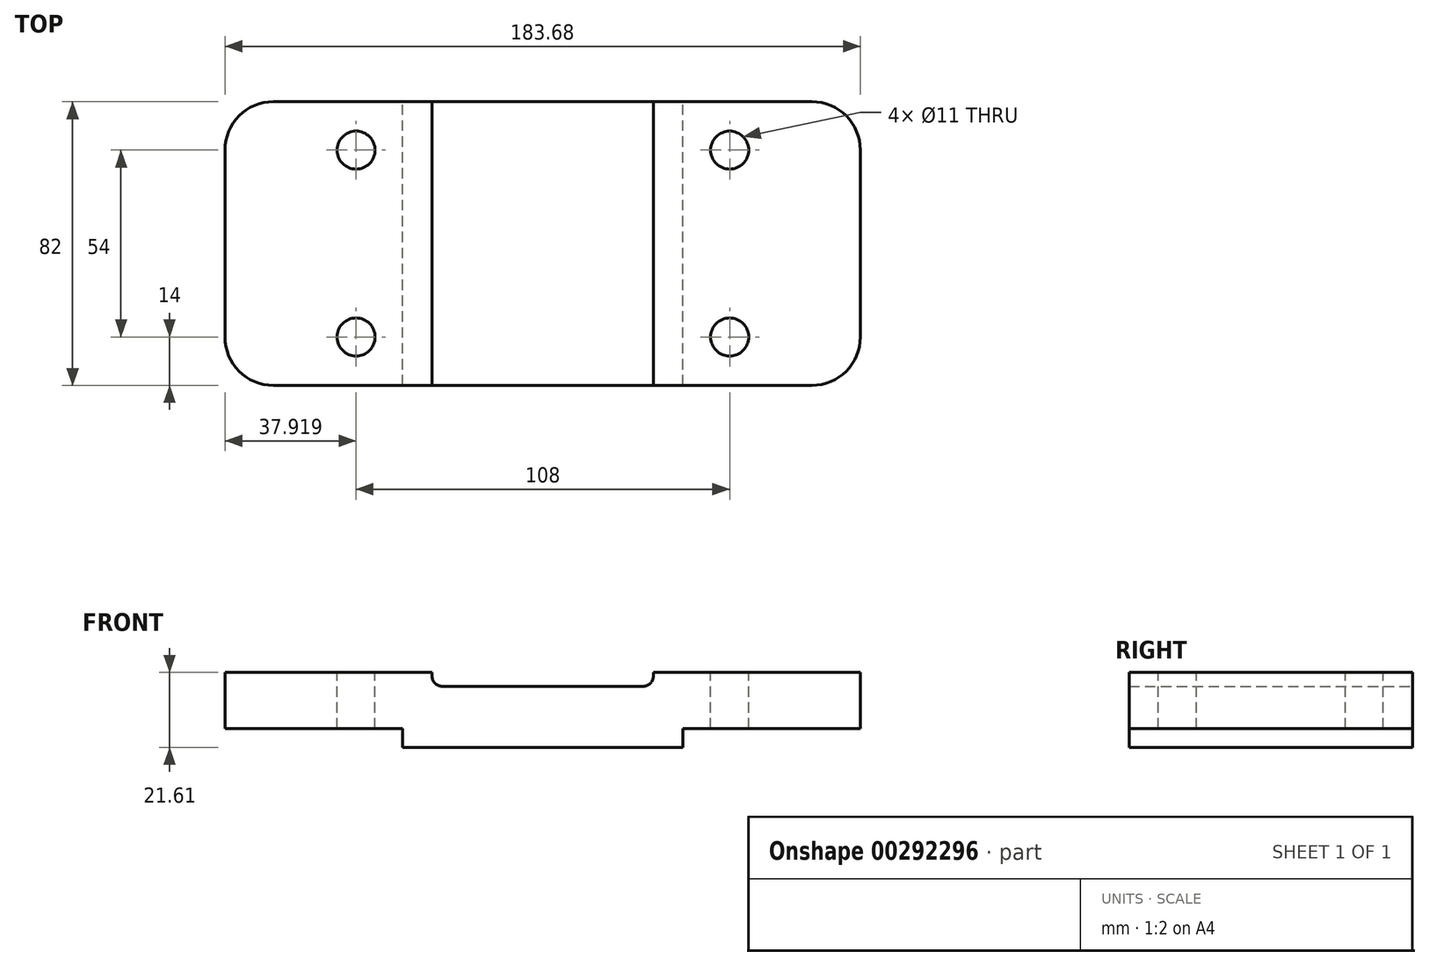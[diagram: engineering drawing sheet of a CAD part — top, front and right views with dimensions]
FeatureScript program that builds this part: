
annotation { "Feature Type Name" : "Feature", "Feature Type Description" : "" }
export const myFeature = defineFeature(function(context is Context, id is Id, definition is map)
    precondition{}
    {
        {
            var Q0;
            Q0=qCreatedBy(makeId("Front.planeOp"),FACE);
            var sketch = newSketch(context, id + "F0", { "sketchPlane" : qUnion([Q0])});
            skLineSegment(sketch, "E0.bottom", {"start": v(0, 0) * mm, "end": v(0, 0) * mm});
            skLineSegment(sketch, "E1", {"start": v(0, 0) * mm, "end": v(0, 21.6) * mm});
            skLineSegment(sketch, "E2", {"start": v(0, 21.6) * mm, "end": v(59.84, 21.6) * mm});
            skLineSegment(sketch, "E3", {"start": v(183.68, 21.6) * mm, "end": v(183.68, 5.4) * mm});
            skLineSegment(sketch, "E4", {"start": v(132.36, 0) * mm, "end": v(51.32, 0) * mm});
            skLineSegment(sketch, "E5", {"start": v(91.84, 21.6) * mm, "end": v(91.84, 0) * mm, "construction": true});
            skLineSegment(sketch, "E6.top", {"start": v(0, 5.4) * mm, "end": v(51.32, 5.4) * mm});
            skLineSegment(sketch, "E6.right", {"start": v(51.32, 0) * mm, "end": v(51.32, 5.4) * mm});
            skLineSegment(sketch, "E7.top", {"start": v(183.68, 5.4) * mm, "end": v(132.36, 5.4) * mm});
            skLineSegment(sketch, "E7.right", {"start": v(132.36, 0) * mm, "end": v(132.36, 5.4) * mm});
            skPoint(sketch, "E8.orphan", {"position": v(183.68, 0) * mm});
            skLineSegment(sketch, "E9", {"start": v(123.84, 21.6) * mm, "end": v(123.84, 20.6) * mm});
            skLineSegment(sketch, "E10", {"start": v(120.84, 17.6) * mm, "end": v(62.88, 17.6) * mm});
            skLineSegment(sketch, "E11", {"start": v(59.88, 20.51) * mm, "end": v(59.84, 21.6) * mm});
            skPoint(sketch, "E12.MirrorCS.end.orphan", {"position": v(91.84, 21.6) * mm});
            skPoint(sketch, "E12.MirrorCS.start.orphan", {"position": v(123.84, 21.6) * mm});
            skPoint(sketch, "E13.MirrorCS.start.orphan", {"position": v(59.84, 21.6) * mm});
            skLineSegment(sketch, "E14.trimOffspring", {"start": v(123.84, 21.6) * mm, "end": v(183.68, 21.6) * mm});
            skPoint(sketch, "E15.visualSharp", {"position": v(123.84, 17.6) * mm});
            skArc(sketch, "E15.filletArc", {"start": v(120.84, 17.6) * mm, "mid": v(122.96, 18.49) * mm, "end": v(123.84, 20.6) * mm});
            skPoint(sketch, "E16.visualSharp", {"position": v(59.97, 17.6) * mm});
            skArc(sketch, "E16.filletArc", {"start": v(59.88, 20.51) * mm, "mid": v(60.79, 18.46) * mm, "end": v(62.88, 17.6) * mm});
            skSolve(sketch);
        }
        {
            var Q0;
            {var subQ1=sQuery(id+"F0.wireOp",EDGE,"E2");Q0=makeQuery(id+"F0.imprint","IMPRINT",FACE,{"disambiguationData":[TD([[makeQuery(id+"F0.imprint","IMPRINT",EDGE,{"derivedFrom":subQ1}),-1.0]])]});}
            extrude(context, id + "F1", {"entities" : qUnion([Q0]), "depth" : 82 * mm});
        }
        {
            var Q0;
            Q0=makeQuery(id+"F1.opExtrude","CAP_EDGE",EDGE,{"disambiguationData":[OSD([sQuery(id+"F0.wireOp",EDGE,"E1")])],"isStart":false});
            var Q1;
            Q1=makeQuery(id+"F1.opExtrude","CAP_EDGE",EDGE,{"disambiguationData":[OSD([sQuery(id+"F0.wireOp",EDGE,"E3")])],"isStart":false});
            var Q2;
            Q2=makeQuery(id+"F1.opExtrude","CAP_EDGE",EDGE,{"disambiguationData":[OSD([sQuery(id+"F0.wireOp",EDGE,"E3")])],"isStart":true});
            var Q3;
            Q3=makeQuery(id+"F1.opExtrude","CAP_EDGE",EDGE,{"disambiguationData":[OSD([sQuery(id+"F0.wireOp",EDGE,"E1")])],"isStart":true});
            fillet(context, id + "F2", {"entities" : qUnion([Q0, Q1, Q2, Q3]), "radius" : 14 * mm, "tangentPropagation" : true, "allowEdgeOverflow" : false});
        }
        {
            var Q0;
            Q0=makeQuery(id+"F1.opExtrude","SWEPT_FACE",FACE,{"disambiguationData":[OSD([sQuery(id+"F0.wireOp",EDGE,"E2")])]});
            var sketch = newSketch(context, id + "F3", { "sketchPlane" : qUnion([Q0])});
            skPoint(sketch, "E17.endSnap0", {"position": v(59.84, -41) * mm});
            skLineSegment(sketch, "E18.bottom", {"start": v(145.92, -14) * mm, "end": v(37.92, -14) * mm, "construction": true});
            skLineSegment(sketch, "E18.top", {"start": v(145.92, -68) * mm, "end": v(37.92, -68) * mm, "construction": true});
            skLineSegment(sketch, "E18.left", {"start": v(145.92, -14) * mm, "end": v(145.92, -68) * mm, "construction": true});
            skLineSegment(sketch, "E18.right", {"start": v(37.92, -14) * mm, "end": v(37.92, -68) * mm, "construction": true});
            skPoint(sketch, "E18.middle", {"position": v(91.92, -41) * mm});
            skCircle(sketch, "E19", {"center": v(37.92, -14) * mm, "radius": 5.5 * mm});
            skCircle(sketch, "E20", {"center": v(145.92, -14) * mm, "radius": 5.5 * mm});
            skCircle(sketch, "E21", {"center": v(145.92, -68) * mm, "radius": 5.5 * mm});
            skCircle(sketch, "E22", {"center": v(37.92, -68) * mm, "radius": 5.5 * mm});
            skSolve(sketch);
        }
        {
            var Q0;
            Q0 = qSketchRegion(id + "F3", true);
            extrude(context, id + "F4", {"entities" : qUnion([Q0]), "operationType" : NewBodyOperationType.REMOVE, "endBound" : BoundingType.THROUGH_ALL, "oppositeDirection" : true, "depth" : 25 * mm});
        }
    });
